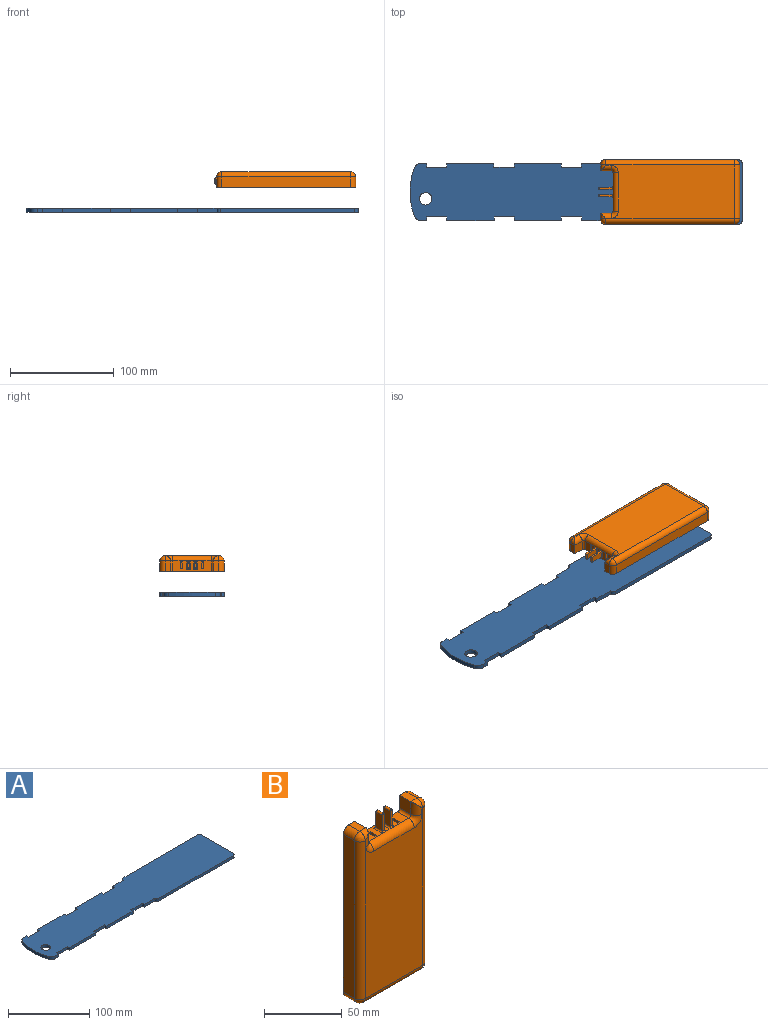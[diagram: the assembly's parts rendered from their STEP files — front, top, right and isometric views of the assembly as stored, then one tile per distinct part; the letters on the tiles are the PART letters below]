
ASSEMBLY  parts=2 mates=1
PART A: 41 faces, bbox 320x62x4 mm
  f0: cylinder r=66.02mm len=45.86mm, axis (0,0,-1), area 187.4mm2, adj f1,f34,f35,f36
  f1: cylinder r=7mm len=6.56mm, axis (0,0,-1), area 34mm2, adj f0,f2,f35,f36
  f2: plane 5.33x4mm, normal (0,-1,0), area 21.3mm2, adj f1,f3,f35,f36
  f3: plane 4x3.6mm, normal (1,0,0), area 14.4mm2, adj f2,f4,f35,f36
  f4: plane 19.5x4mm, normal (0,-1,0), area 78mm2, adj f3,f5,f35,f36
  f5: plane 4x3.6mm, normal (-1,0,0), area 14.4mm2, adj f4,f6,f35,f36
  f6: plane 45.57x4mm, normal (0,-1,0), area 182.3mm2, adj f5,f7,f35,f36
  f7: plane 4x3.6mm, normal (1,0,0), area 14.4mm2, adj f6,f8,f35,f36
  f8: plane 19.5x4mm, normal (0,-1,0), area 78mm2, adj f7,f9,f35,f36
  f9: plane 4x3.6mm, normal (-1,0,0), area 14.4mm2, adj f8,f10,f35,f36
  f10: plane 45.4x4mm, normal (0,-1,0), area 181.6mm2, adj f9,f11,f35,f36
  f11: plane 4x3.6mm, normal (1,0,0), area 14.4mm2, adj f10,f12,f35,f36
  f12: plane 19.5x4mm, normal (0,-1,0), area 78mm2, adj f11,f13,f35,f36
  f13: plane 4x3.6mm, normal (-1,0,0), area 14.4mm2, adj f12,f14,f35,f36
  f14: plane 18.7x4mm, normal (0,-1,0), area 74.8mm2, adj f13,f15,f35,f36
  f15: plane 4x0.5mm, normal (-1,0,0), area 2mm2, adj f14,f35,f36,f37
  f16: plane 129.83x4mm, normal (0,-1,0), area 519.3mm2, adj f35,f36,f37,f38
  f17: plane 56x4mm, normal (1,0,0), area 224mm2, adj f35,f36,f38,f39
  f18: plane 129.97x4mm, normal (0,1,0), area 519.9mm2, adj f35,f36,f39,f40
  f19: plane 4x0.65mm, normal (-1,0.05,0), area 2.6mm2, adj f20,f35,f36,f40
  f20: plane 18.7x4mm, normal (0,1,0), area 74.8mm2, adj f19,f21,f35,f36
  f21: plane 4x3.6mm, normal (-1,0,0), area 14.4mm2, adj f20,f22,f35,f36
  f22: plane 19.5x4mm, normal (0,1,0), area 78mm2, adj f21,f23,f35,f36
  f23: plane 4x3.6mm, normal (1,0,0), area 14.4mm2, adj f22,f24,f35,f36
  f24: plane 45.4x4mm, normal (0,1,0), area 181.6mm2, adj f23,f25,f35,f36
  f25: plane 4x3.6mm, normal (-1,0,0), area 14.4mm2, adj f24,f26,f35,f36
  f26: plane 19.5x4mm, normal (0,1,0), area 78mm2, adj f25,f27,f35,f36
  f27: plane 4x3.6mm, normal (1,0,0), area 14.4mm2, adj f26,f28,f35,f36
  f28: plane 45.4x4mm, normal (0,1,0), area 181.6mm2, adj f27,f29,f35,f36
  f29: plane 4x3.6mm, normal (-1,0,0), area 14.4mm2, adj f28,f30,f35,f36
  f30: plane 19.5x4mm, normal (0,1,0), area 78mm2, adj f29,f31,f35,f36
  f31: plane 4x3.6mm, normal (1,0,0), area 14.4mm2, adj f30,f32,f35,f36
  f32: plane 5.33x4mm, normal (0,1,0), area 21.3mm2, adj f31,f34,f35,f36
  f33: cylinder r=6mm len=12mm, axis (0,0,-1), area 150.8mm2, adj f35,f36
  f34: cylinder r=7mm len=6.56mm, axis (0,0,-1), area 34mm2, adj f0,f32,f35,f36
  f35: plane 320x62mm, normal (0,0,1), area 17893.3mm2, adj f0,f1,f2,f3,f4,f5,f6,f7
  f36: plane 320x62mm, normal (0,0,-1), area 17893.3mm2, adj f0,f1,f2,f3,f4,f5,f6,f7
  f37: cylinder r=3mm len=4mm, axis (0,0,1), area 18.8mm2, adj f15,f16,f35,f36
  f38: cylinder r=3mm len=4mm, axis (0,0,1), area 18.8mm2, adj f16,f17,f35,f36
  f39: cylinder r=3mm len=4mm, axis (0,0,-1), area 18.8mm2, adj f17,f18,f35,f36
  f40: cylinder r=3mm len=4mm, axis (0,0,1), area 18.3mm2, adj f18,f19,f35,f36
PART B: 77 faces, bbox 62x15x136 mm
  f0: plane 134x62mm, normal (0,1,0), area 1261.7mm2, adj f10,f11,f20,f21,f22,f23,f24,f25
  f1: plane 6x6mm, normal (1,0,0), area 36mm2, adj f2,f7,f10,f11,f65
  f2: plane 6x2mm, normal (0,-1,0), area 12mm2, adj f1,f3,f10,f11
  f3: plane 6x6mm, normal (-1,0,0), area 36mm2, adj f2,f7,f10,f11,f65
  f4: plane 6x2mm, normal (0,-1,0), area 12mm2, adj f5,f8,f10,f11
  f5: plane 6x6mm, normal (-1,0,0), area 36mm2, adj f4,f6,f10,f11,f65
  f6: plane 6x2mm, normal (0,1,0), area 12mm2, adj f5,f8,f10,f65
  f7: plane 6x2mm, normal (0,1,0), area 12mm2, adj f1,f3,f10,f65
  f8: plane 6x6mm, normal (1,0,0), area 36mm2, adj f4,f6,f10,f11,f65
  f9: plane 124x52mm, normal (0,-1,0), area 5857mm2, adj f47,f48,f49,f50,f51,f52,f53,f54
  f10: plane 37x10mm, normal (0,0,1), area 282mm2, adj f0,f1,f2,f3,f4,f5,f6,f7
  f11: plane 49.6x8.8mm, normal (0,0,-1), area 413.3mm2, adj f0,f1,f2,f3,f4,f5,f8,f58
  f12: plane 12x2mm, normal (0,-1,0), area 24mm2, adj f13,f15,f29,f38
  f13: plane 12x6mm, normal (-1,0,0), area 72mm2, adj f12,f14,f30,f39
  f14: plane 12x2mm, normal (0,1,0), area 24mm2, adj f13,f15,f31,f37
  f15: plane 12x6mm, normal (1,0,0), area 72mm2, adj f12,f14,f30,f36
  f16: plane 12x6mm, normal (1,0,0), area 72mm2, adj f17,f19,f27,f34
  f17: plane 12x2mm, normal (0,-1,0), area 24mm2, adj f16,f18,f28,f35
  f18: plane 12x6mm, normal (-1,0,0), area 72mm2, adj f17,f19,f27,f33
  f19: plane 12x2mm, normal (0,1,0), area 24mm2, adj f16,f18,f26,f32
  f20: plane 10x10mm, normal (-1,0,0), area 100mm2, adj f0,f22,f41,f50
  f21: plane 124x10mm, normal (1,0,0), area 1240mm2, adj f0,f54,f69,f75
  f22: plane 10x5.5mm, normal (0,0,1), area 55mm2, adj f0,f20,f52,f75
  f23: plane 10x10mm, normal (1,0,0), area 100mm2, adj f0,f25,f40,f51
  f24: plane 124x10mm, normal (-1,0,0), area 1240mm2, adj f0,f55,f71,f73
  f25: plane 10x5.5mm, normal (0,0,1), area 55mm2, adj f0,f23,f53,f73
  f26: cylinder r=1mm len=2mm, axis (1,0,0), area 2mm2, adj f19,f27
  f27: cylinder r=1mm len=6mm, axis (0,1,0), area 16.6mm2, adj f16,f18,f26,f28
  f28: cylinder r=1mm len=2mm, axis (-1,0,0), area 2mm2, adj f17,f27
  f29: cylinder r=1mm len=2mm, axis (-1,0,0), area 2mm2, adj f12,f30
  f30: cylinder r=1mm len=6mm, axis (0,-1,0), area 16.6mm2, adj f13,f15,f29,f31
  f31: cylinder r=1mm len=2mm, axis (1,0,0), area 2mm2, adj f14,f30
  f32: cylinder r=1mm len=4mm, axis (-1,0,0), area 4.3mm2, adj f10,f19,f33,f34
  f33: cylinder r=1mm len=8mm, axis (0,-1,0), area 10.6mm2, adj f10,f18,f32,f35
  f34: cylinder r=1mm len=8mm, axis (0,1,0), area 10.6mm2, adj f10,f16,f32,f35
  f35: cylinder r=1mm len=4mm, axis (1,0,0), area 4.3mm2, adj f17,f33,f34,f47
  f36: cylinder r=1mm len=8mm, axis (0,1,0), area 10.6mm2, adj f10,f15,f37,f38
  f37: cylinder r=1mm len=4mm, axis (-1,0,0), area 4.3mm2, adj f10,f14,f36,f39
  f38: cylinder r=1mm len=4mm, axis (1,0,0), area 4.3mm2, adj f12,f36,f39,f47
  f39: cylinder r=1mm len=8mm, axis (0,-1,0), area 10.6mm2, adj f10,f13,f37,f38
  f40: cylinder r=2mm len=10mm, axis (0,1,0), area 31.4mm2, adj f0,f10,f23,f49
  f41: cylinder r=2mm len=10mm, axis (0,-1,0), area 31.4mm2, adj f0,f10,f20,f48
  f42: plane 100x49.6mm, normal (0,1,0), area 4960mm2, adj f59,f62,f65,f68
  f43: plane 100x8.8mm, normal (-1,0,0), area 880mm2, adj f0,f63,f64,f68
  f44: plane 100x8.8mm, normal (1,0,0), area 880mm2, adj f0,f57,f58,f59
  f45: plane 49.6x8.8mm, normal (0,0,1), area 436.5mm2, adj f0,f57,f62,f63
  f46: plane 52x10mm, normal (0,0,-1), area 520mm2, adj f0,f56,f69,f71
  f47: cylinder r=5mm len=37mm, axis (-1,0,0), area 290.6mm2, adj f9,f10,f35,f38,f48,f49
  f48: torus R=7mm, axis (0,-1,0), area 47.1mm2, adj f9,f41,f47,f50
  f49: torus R=7mm, axis (0,-1,0), area 47.1mm2, adj f9,f40,f47,f51
  f50: cylinder r=5mm len=10mm, axis (0,0,-1), area 64.3mm2, adj f9,f20,f48,f52
  f51: cylinder r=5mm len=10mm, axis (0,0,1), area 64.3mm2, adj f9,f23,f49,f53
  f52: cylinder r=5mm len=5.5mm, axis (1,0,0), area 28.9mm2, adj f9,f22,f50,f76
  f53: cylinder r=5mm len=5.5mm, axis (-1,0,0), area 28.9mm2, adj f9,f25,f51,f74
  f54: cylinder r=5mm len=124mm, axis (0,0,1), area 973.9mm2, adj f9,f21,f70,f76
  f55: cylinder r=5mm len=124mm, axis (0,0,-1), area 973.9mm2, adj f9,f24,f72,f74
  f56: cylinder r=5mm len=52mm, axis (-1,0,0), area 408.4mm2, adj f9,f46,f70,f72
  f57: cylinder r=5mm len=8.8mm, axis (0,1,0), area 69.1mm2, adj f0,f44,f45,f60
  f58: cylinder r=5mm len=8.8mm, axis (0,1,0), area 69.1mm2, adj f0,f11,f44,f61
  f59: cylinder r=5mm len=100mm, axis (0,0,-1), area 785.4mm2, adj f42,f44,f60,f61
  f60: sphere r=5mm, area 39.3mm2, adj f57,f59,f62
  f61: sphere r=5mm, area 39.3mm2, adj f58,f59,f65
  f62: cylinder r=5mm len=49.6mm, axis (-1,0,0), area 389.6mm2, adj f42,f45,f60,f66
  f63: cylinder r=5mm len=8.8mm, axis (0,-1,0), area 69.1mm2, adj f0,f43,f45,f66
  f64: cylinder r=5mm len=8.8mm, axis (0,-1,0), area 69.1mm2, adj f0,f11,f43,f67
  f65: cylinder r=5mm len=49.6mm, axis (-1,0,0), area 388.8mm2, adj f1,f3,f5,f6,f7,f8,f11,f42
  f66: sphere r=5mm, area 39.3mm2, adj f62,f63,f68
  f67: sphere r=5mm, area 39.3mm2, adj f64,f65,f68
  f68: cylinder r=5mm len=100mm, axis (0,0,1), area 785.4mm2, adj f42,f43,f66,f67
  f69: cylinder r=5mm len=10mm, axis (0,-1,0), area 78.5mm2, adj f0,f21,f46,f70
  f70: sphere r=5mm, area 39.3mm2, adj f54,f56,f69
  f71: cylinder r=5mm len=10mm, axis (0,1,0), area 78.5mm2, adj f0,f24,f46,f72
  f72: sphere r=5mm, area 39.3mm2, adj f55,f56,f71
  f73: cylinder r=5mm len=10mm, axis (0,1,0), area 78.5mm2, adj f0,f24,f25,f74
  f74: sphere r=5mm, area 39.3mm2, adj f53,f55,f73
  f75: cylinder r=5mm len=10mm, axis (0,-1,0), area 78.5mm2, adj f0,f21,f22,f76
  f76: sphere r=5mm, area 39.3mm2, adj f52,f54,f75
PLACE A at identity fixed
PLACE B rot(axis=(-0.58,-0.58,0.58),120deg) t=(131.79,0.04,31.5)mm
MATE parallel B.f0 <-> A.f35  axis (0,0,-1) through (173.42,0.04,24)mm
